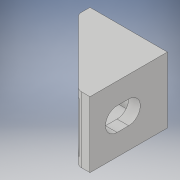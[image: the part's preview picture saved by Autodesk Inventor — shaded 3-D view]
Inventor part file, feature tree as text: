
AUTODESK INVENTOR PART (.ipt)
format: ipt  version: 2018 (Build 220112000, 112)  size: 144,384 bytes
history: native  units: in
note: dims shown in document units (in); Inventor stores cm internally (conversion verified against a paired STEP export)
features: extrude x4, sketch x4, mirror x1, fillet x1
ambient origin geometry x8: Origin, YZ Plane, XZ Plane, XY Plane, X Axis, Y Axis, Z Axis, Center Point
bodies: Solid1 (feature_tree)
feature tree (10):
  extrude  "Extrusion1"  Depth=0.7874in
  extrude  "Extrusion2"  Depth=0.1181in
  extrude  "Extrusion3"  Depth=0.2362in
  extrude  "Extrusion4"  Depth=0.7874in TaperAngle=0.0deg
  mirror  "Mirror1"
  fillet  "Fillet1"  Radius=0.2362in
  sketch  "Sketch1"  dims[d0=0.7874in d1=0.7874in]
  sketch  "Sketch2"  dims[d2=0.1181in d3=0.1181in]
  sketch  "Sketch3"  dims[d4=0.6693in d5=0.0in d6=0.2362in]
  sketch  "Sketch4"  dims[d7=0.1181in d8=0.7874in d9=0.0in d10=0.2362in d11=0.1181in d12=0.7874in d13=0.0in d14=0.0787in d15=0.0in d16=0.0787in]
